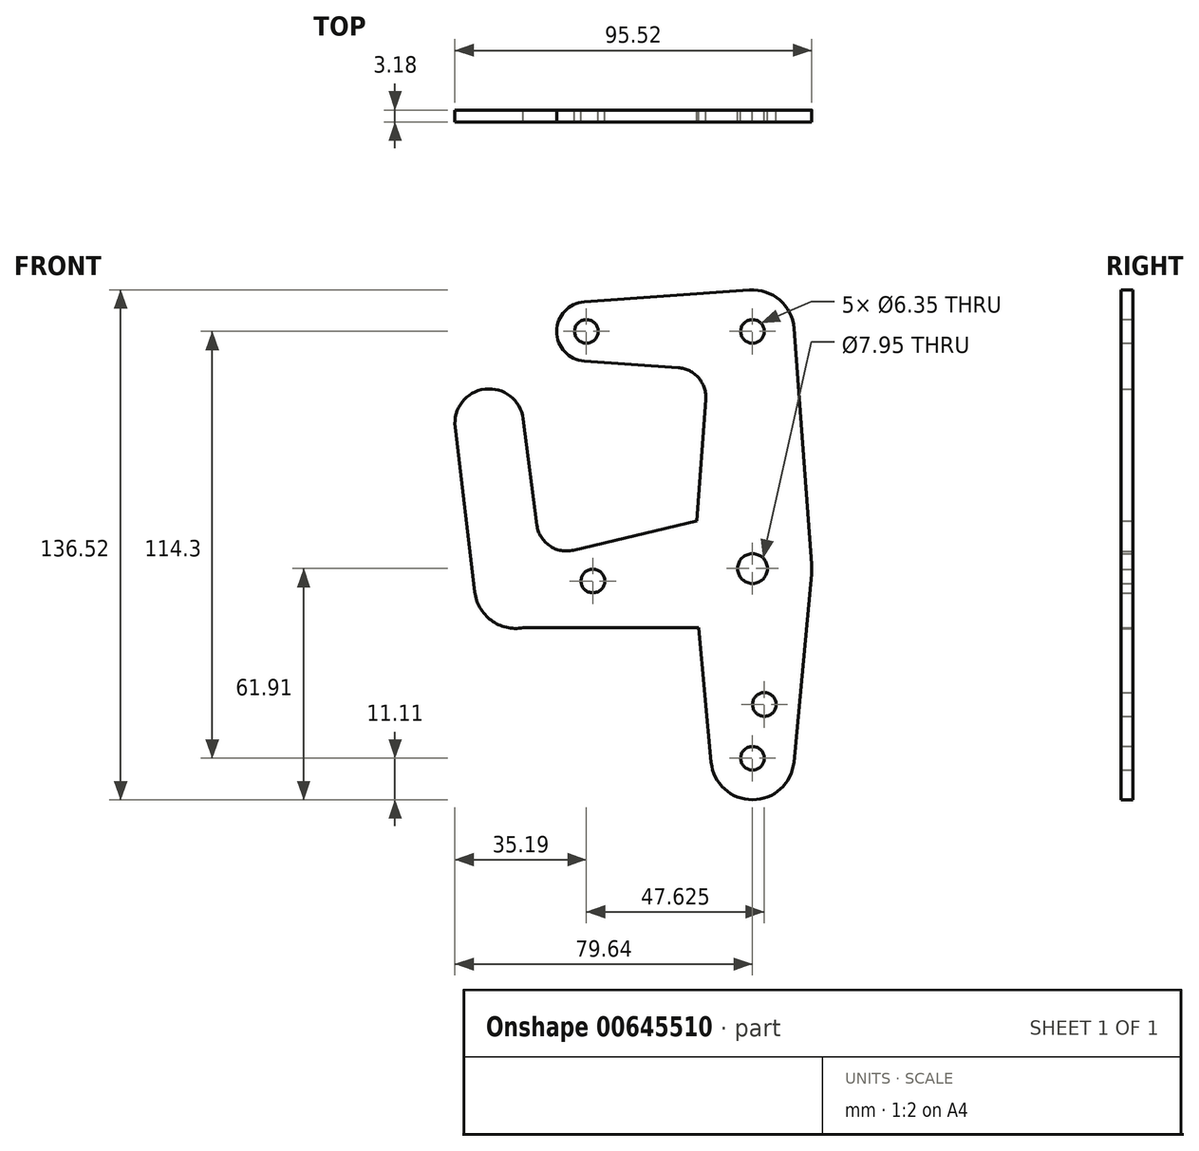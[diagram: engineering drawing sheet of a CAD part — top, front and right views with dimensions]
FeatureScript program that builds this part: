
annotation { "Feature Type Name" : "Feature", "Feature Type Description" : "" }
export const myFeature = defineFeature(function(context is Context, id is Id, definition is map)
    precondition{}
    {
        {
            var Q0;
            Q0=qCreatedBy(makeId("Front.planeOp"),FACE);
            var sketch = newSketch(context, id + "F0", { "sketchPlane" : qUnion([Q0])});
            skCircle(sketch, "E0", {"center": v(-44.45, 63.5) * mm, "radius": 7.94 * mm});
            skCircle(sketch, "E1", {"center": v(0, 63.5) * mm, "radius": 11.11 * mm});
            skCircle(sketch, "E2", {"center": v(0, 0) * mm, "radius": 15.88 * mm});
            skCircle(sketch, "E3", {"center": v(0, -50.8) * mm, "radius": 11.11 * mm});
            skLineSegment(sketch, "E4", {"start": v(-44.45, 63.5) * mm, "end": v(0, 63.5) * mm, "construction": true});
            skLineSegment(sketch, "E5", {"start": v(0, 63.5) * mm, "end": v(0, 0) * mm, "construction": true});
            skLineSegment(sketch, "E6", {"start": v(0, -50.8) * mm, "end": v(0, 0) * mm, "construction": true});
            skCircle(sketch, "E7", {"center": v(-44.45, 63.5) * mm, "radius": 3.18 * mm});
            skCircle(sketch, "E8", {"center": v(0, 0) * mm, "radius": 3.98 * mm});
            skCircle(sketch, "E9", {"center": v(0, -50.8) * mm, "radius": 3.18 * mm});
            skCircle(sketch, "E10", {"center": v(0, 63.5) * mm, "radius": 3.18 * mm});
            skCircle(sketch, "E11", {"center": v(3.18, -36.39) * mm, "radius": 3.18 * mm});
            skLineSegment(sketch, "E12", {"start": v(-45.02, 71.42) * mm, "end": v(-0.8, 74.58) * mm});
            skLineSegment(sketch, "E13", {"start": v(-45.02, 55.58) * mm, "end": v(-19.88, 53.78) * mm});
            skCircle(sketch, "E14", {"center": v(0, 0) * mm, "radius": 3.05 * mm});
            skLineSegment(sketch, "E15", {"start": v(-12.52, 45.26) * mm, "end": v(-15.83, 1.2) * mm});
            skLineSegment(sketch, "E16", {"start": v(-15.8, -1.49) * mm, "end": v(-11.06, -51.84) * mm});
            skLineSegment(sketch, "E17", {"start": v(11.08, 64.33) * mm, "end": v(15.83, 1.2) * mm});
            skLineSegment(sketch, "E18", {"start": v(15.8, -1.49) * mm, "end": v(11.06, -51.84) * mm});
            skArc(sketch, "E19.filletArc", {"start": v(-12.52, 45.26) * mm, "mid": v(-14.43, 51.05) * mm, "end": v(-19.88, 53.78) * mm});
            skCircle(sketch, "E20", {"center": v(-63.3, -4.93) * mm, "radius": 11.11 * mm});
            skLineSegment(sketch, "E21", {"start": v(-61.39, -15.88) * mm, "end": v(0, -15.88) * mm});
            skLineSegment(sketch, "E22", {"start": v(-47.95, 4.9) * mm, "end": v(-3.68, 15.44) * mm});
            skCircle(sketch, "E23", {"center": v(-70.47, 38.94) * mm, "radius": 9.17 * mm});
            skLineSegment(sketch, "E24", {"start": v(-63.3, -4.93) * mm, "end": v(0, 0) * mm, "construction": true});
            skLineSegment(sketch, "E25", {"start": v(-70.47, 38.94) * mm, "end": v(-63.3, -4.93) * mm, "construction": true});
            skLineSegment(sketch, "E26", {"start": v(-74.34, -6.24) * mm, "end": v(-79.58, 37.86) * mm});
            skLineSegment(sketch, "E27", {"start": v(-57.68, 11.62) * mm, "end": v(-61.38, 40.12) * mm});
            skArc(sketch, "E28.filletArc", {"start": v(-57.68, 11.62) * mm, "mid": v(-54.3, 6.1) * mm, "end": v(-47.95, 4.9) * mm});
            skCircle(sketch, "E29", {"center": v(-42.72, -3.33) * mm, "radius": 3.18 * mm});
            skSolve(sketch);
        }
        {
            var Q0;
            Q0 = qSketchRegion(id + "F0", true);
            extrude(context, id + "F1", {"entities" : qUnion([Q0]), "depth" : 3.17 * mm, "offsetDistance" : 25.4 * mm});
        }
    });
